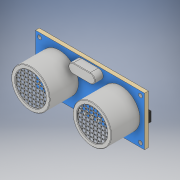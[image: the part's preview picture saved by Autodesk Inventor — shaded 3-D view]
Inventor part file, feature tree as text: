
AUTODESK INVENTOR PART (.ipt)
format: ipt  version: 2019 (Build 230136000, 136)  size: 352,768 bytes
history: native  units: mm
features: extrude x9, sketch x9, projected_geometry x6, chamfer x5, other x1, fillet x1
ambient origin geometry x8: Origin, YZ Plane, XZ Plane, XY Plane, X Axis, Y Axis, Z Axis, Center Point
bodies: Body1 (feature_tree)
feature tree (31):
  other  "Твердое тело1"
  extrude  "Выдавливание1"  Depth=45.4mm
  extrude  "Выдавливание2"  Depth=20.4mm
  extrude  "Выдавливание3"  Depth=42.0mm
  chamfer  "Фаска1"  Distance=17.0mm
  extrude  "Выдавливание4"  Depth=1.6mm
  extrude  "Выдавливание5"  Depth=1.6mm TaperAngle=0.0deg
  fillet  "Сопряжение1"  Radius=16.0mm
  extrude  "Выдавливание7"  Depth=25.6mm
  extrude  "Выдавливание8"  Depth=12.0mm TaperAngle=0.0deg
  chamfer  "Фаска2"  Distance=1.6mm
  extrude  "Выдавливание9"  Depth=0.4mm TaperAngle=0.0deg
  chamfer  "Фаска3"  Distance=2.0mm Angle=45.0deg
  extrude  "Выдавливание10"  Depth=7.0mm
  chamfer  "Фаска4"  Distance=2.0mm
  chamfer  "Фаска5"  Distance=2.5mm
  sketch  "Эскиз1"
  sketch  "Эскиз2"
  sketch  "Эскиз3"
  projected_geometry  "Спроецированная петля1"
  projected_geometry  "Спроецированная петля2"
  sketch  "Эскиз4"
  sketch  "Эскиз5"
  sketch  "Эскиз7"
  sketch  "Эскиз8"
  projected_geometry  "Спроецированная петля3"
  sketch  "Эскиз9"
  projected_geometry  "Спроецированная петля4"
  projected_geometry  "Спроецированная петля5"
  projected_geometry  "Спроецированная петля6"
  sketch  "Эскиз10"
